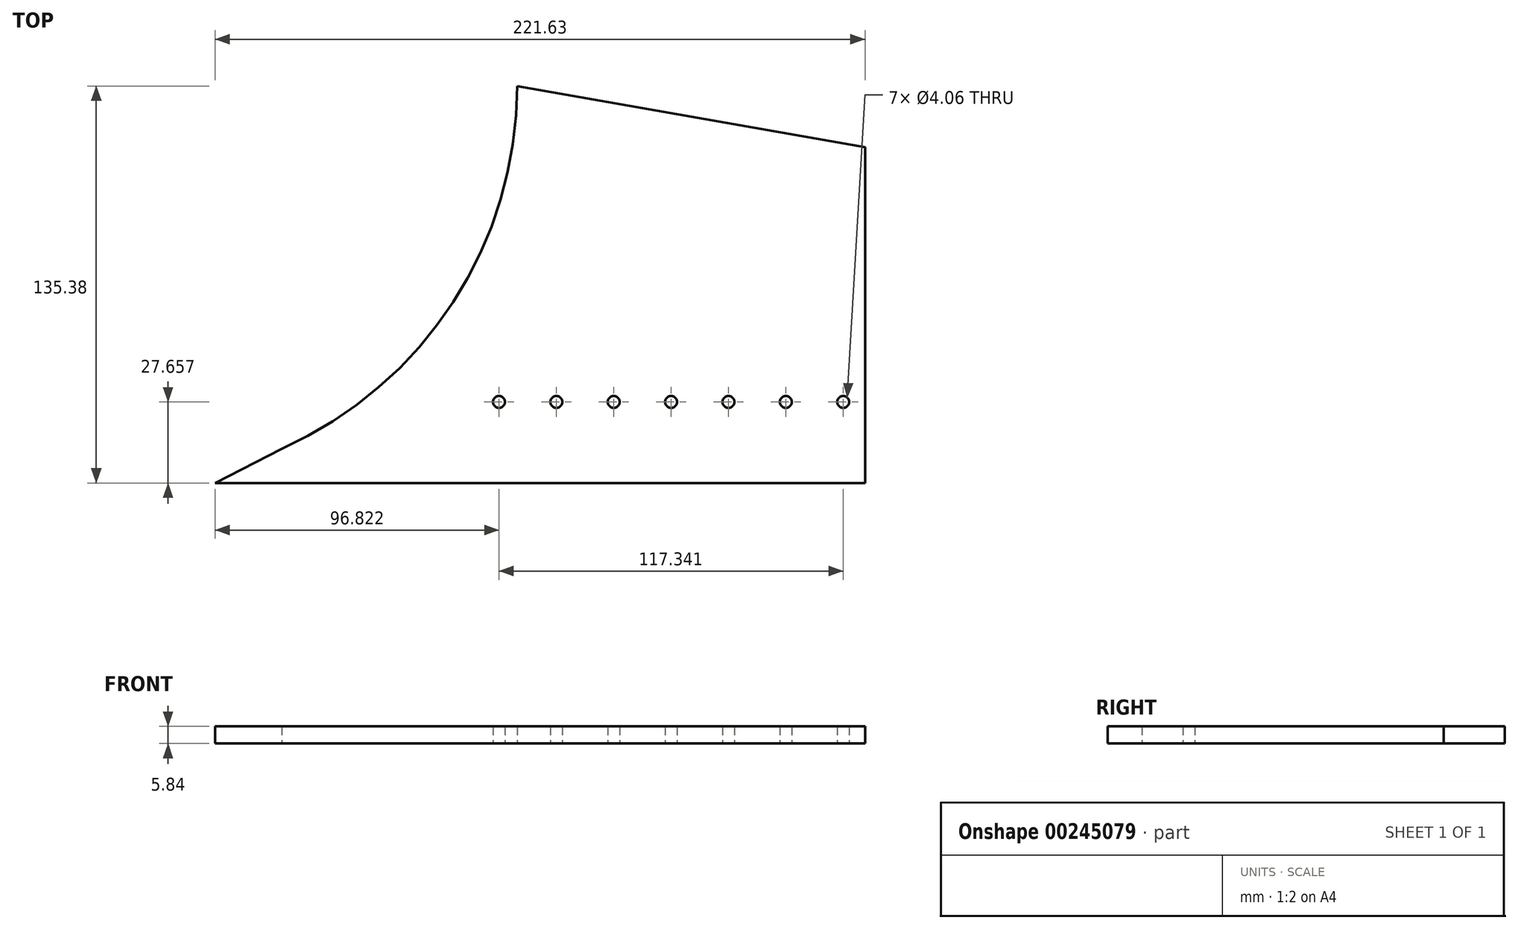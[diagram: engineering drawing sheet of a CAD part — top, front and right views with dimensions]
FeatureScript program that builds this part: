
annotation { "Feature Type Name" : "Feature", "Feature Type Description" : "" }
export const myFeature = defineFeature(function(context is Context, id is Id, definition is map)
    precondition{}
    {
        {
            var Q0;
            Q0=qCreatedBy(makeId("Top.planeOp"),FACE);
            var sketch = newSketch(context, id + "F0", { "sketchPlane" : qUnion([Q0])});
            skArc(sketch, "E0", {"start": v(55.1, -123.67) * mm, "mid": v(113.55, -73.72) * mm, "end": v(135.38, 0) * mm});
            skLineSegment(sketch, "E1.top", {"start": v(32.37, -135.38) * mm, "end": v(254, -135.38) * mm});
            skLineSegment(sketch, "E1.right", {"start": v(254, -20.8) * mm, "end": v(254, -135.38) * mm});
            skLineSegment(sketch, "E2", {"start": v(135.38, 0) * mm, "end": v(254, -20.8) * mm});
            skLineSegment(sketch, "E3", {"start": v(253.93, -135.38) * mm, "end": v(253.93, -107.98) * mm});
            skLineSegment(sketch, "E4", {"start": v(32.37, -135.38) * mm, "end": v(55.1, -123.67) * mm});
            skPoint(sketch, "E5.orphan", {"position": v(0, -135.38) * mm});
            skSolve(sketch);
        }
        {
            var Q0;
            {var subQ3=sQuery(id+"F0.wireOp",EDGE,"E0");Q0=makeQuery(id+"F0.imprint","IMPRINT",FACE,{"disambiguationData":[TD([[makeQuery(id+"F0.imprint","IMPRINT",EDGE,{"derivedFrom":subQ3}),-1.0]])]});}
            var sketch = newSketch(context, id + "F1", { "sketchPlane" : qUnion([Q0])});
            skCircle(sketch, "E6", {"center": v(207.42, -107.72) * mm, "radius": 2.03 * mm});
            skCircle(sketch, "E7", {"center": v(187.87, -107.72) * mm, "radius": 2.03 * mm});
            skCircle(sketch, "E8", {"center": v(168.3, -107.72) * mm, "radius": 2.03 * mm});
            skCircle(sketch, "E9", {"center": v(148.75, -107.72) * mm, "radius": 2.03 * mm});
            skCircle(sketch, "E10", {"center": v(129.2, -107.72) * mm, "radius": 2.03 * mm});
            skCircle(sketch, "E11", {"center": v(226.98, -107.72) * mm, "radius": 2.03 * mm});
            skCircle(sketch, "E12", {"center": v(246.53, -107.72) * mm, "radius": 2.03 * mm});
            skSolve(sketch);
        }
        {
            var Q0;
            Q0=makeQuery(id+"F1.imprint","IMPRINT",FACE,{"disambiguationData":[TD([[makeQuery(id+"F1.imprint","IMPRINT",EDGE,{"derivedFrom":sQuery(id+"F1.wireOp",EDGE,"E6")}),-1.0]])]});
            extrude(context, id + "F2", {"entities" : qUnion([Q0]), "depth" : 5.84 * mm});
        }
    });
